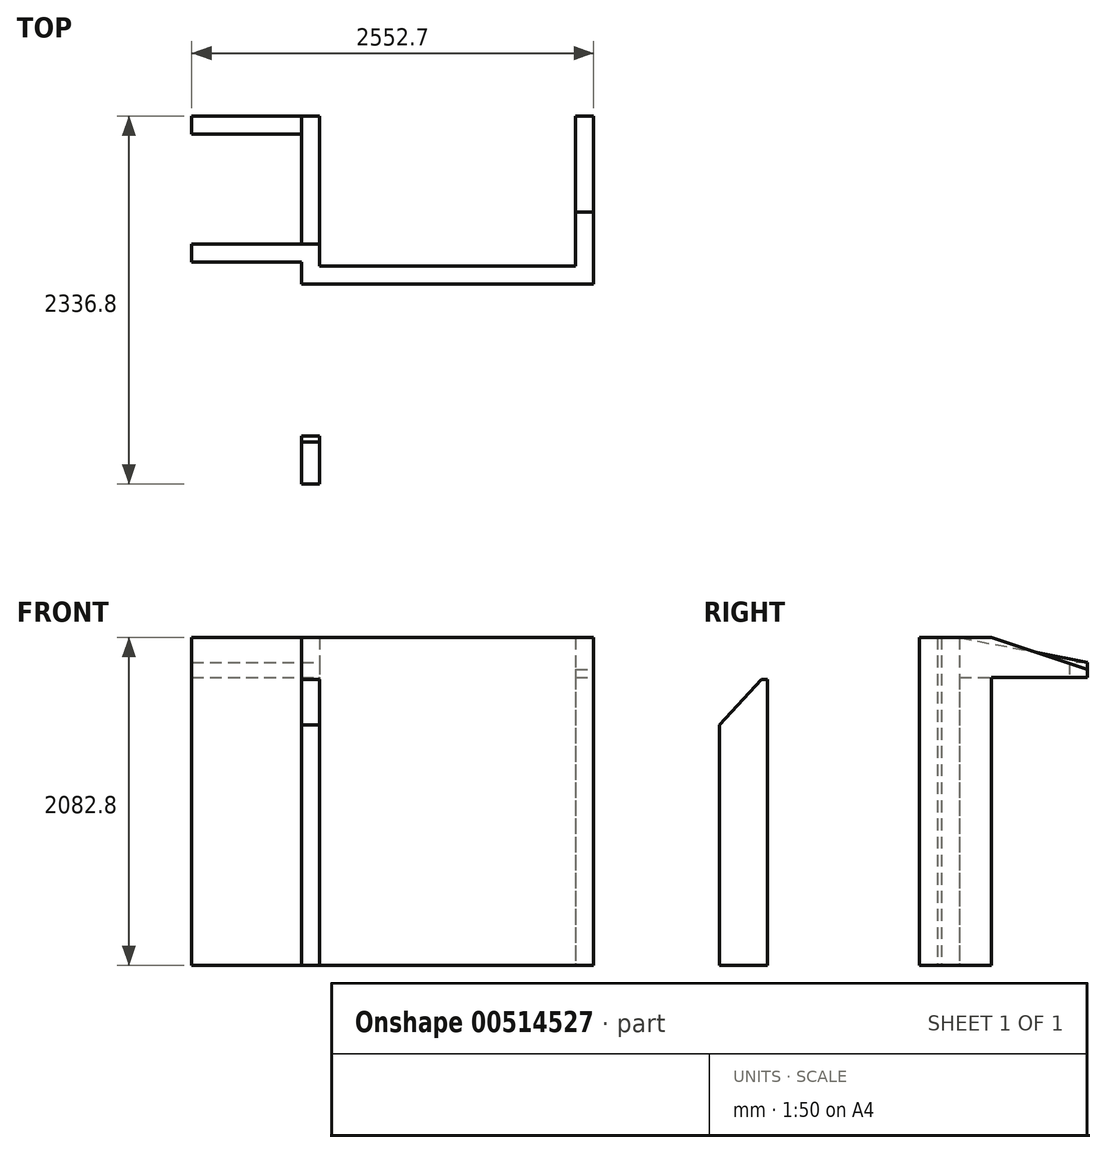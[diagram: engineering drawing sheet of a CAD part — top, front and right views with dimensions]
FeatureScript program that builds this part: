
annotation { "Feature Type Name" : "Feature", "Feature Type Description" : "" }
export const myFeature = defineFeature(function(context is Context, id is Id, definition is map)
    precondition{}
    {
        {
            var Q0;
            Q0=qCreatedBy(makeId("Top.planeOp"),FACE);
            var sketch = newSketch(context, id + "F0", { "sketchPlane" : qUnion([Q0])});
            skLineSegment(sketch, "E0.bottom", {"start": v(0, 0) * mm, "end": v(812.8, 0) * mm});
            skLineSegment(sketch, "E0.top", {"start": v(0, -114.3) * mm, "end": v(812.8, -114.3) * mm});
            skLineSegment(sketch, "E0.left", {"start": v(0, 0) * mm, "end": v(0, -114.3) * mm});
            skLineSegment(sketch, "E0.right", {"start": v(812.8, 0) * mm, "end": v(812.8, -114.3) * mm});
            skLineSegment(sketch, "E1.bottom", {"start": v(812.8, 0) * mm, "end": v(698.5, 0) * mm});
            skLineSegment(sketch, "E1.top", {"start": v(812.8, -254) * mm, "end": v(698.5, -254) * mm});
            skLineSegment(sketch, "E1.left", {"start": v(812.8, 0) * mm, "end": v(812.8, -254) * mm});
            skLineSegment(sketch, "E1.right", {"start": v(698.5, 0) * mm, "end": v(698.5, -254) * mm});
            skLineSegment(sketch, "E2.bottom", {"start": v(698.5, -254) * mm, "end": v(2552.7, -254) * mm});
            skLineSegment(sketch, "E2.top", {"start": v(698.5, -139.7) * mm, "end": v(2552.7, -139.7) * mm});
            skLineSegment(sketch, "E2.left", {"start": v(698.5, -254) * mm, "end": v(698.5, -139.7) * mm});
            skLineSegment(sketch, "E2.right", {"start": v(2552.7, -254) * mm, "end": v(2552.7, -139.7) * mm});
            skLineSegment(sketch, "E3.bottom", {"start": v(2552.7, -254) * mm, "end": v(2438.4, -254) * mm});
            skLineSegment(sketch, "E3.top", {"start": v(2552.7, 203.2) * mm, "end": v(2438.4, 203.2) * mm});
            skLineSegment(sketch, "E3.left", {"start": v(2552.7, -254) * mm, "end": v(2552.7, 203.2) * mm});
            skLineSegment(sketch, "E3.right", {"start": v(2438.4, -254) * mm, "end": v(2438.4, 203.2) * mm});
            skSolve(sketch);
        }
        {
            var Q0;
            Q0 = qSketchRegion(id + "F0", true);
            extrude(context, id + "F1", {"entities" : qUnion([Q0]), "depth" : 2082.8 * mm, "offsetDistance" : 25.4 * mm});
        }
        {
            var Q0;
            Q0=makeQuery(id+"F1.opExtrude","SWEPT_FACE",FACE,{"disambiguationData":[OSD([sQuery(id+"F0.wireOp",EDGE,"E1.right"),sQuery(id+"F0.wireOp",EDGE,"E2.left")])]});
            var sketch = newSketch(context, id + "F2", { "sketchPlane" : qUnion([Q0])});
            skLineSegment(sketch, "E4", {"start": v(254, 0) * mm, "end": v(1219.2, 0) * mm});
            skLineSegment(sketch, "E5.bottom", {"start": v(1219.2, 0) * mm, "end": v(1524, 0) * mm});
            skLineSegment(sketch, "E5.top", {"start": v(1219.2, 1816.1) * mm, "end": v(1524, 1816.1) * mm});
            skLineSegment(sketch, "E5.left", {"start": v(1219.2, 0) * mm, "end": v(1219.2, 1816.1) * mm});
            skLineSegment(sketch, "E5.right", {"start": v(1524, 0) * mm, "end": v(1524, 1816.1) * mm});
            skSolve(sketch);
        }
        {
            var Q0;
            Q0=makeQuery(id+"F2.imprint","IMPRINT",FACE,{"disambiguationData":[TD([[makeQuery(id+"F2.imprint","IMPRINT",EDGE,{"derivedFrom":sQuery(id+"F2.wireOp",EDGE,"E5.bottom")}),1.0]])]});
            extrude(context, id + "F3", {"entities" : qUnion([Q0]), "oppositeDirection" : true, "depth" : 114.3 * mm, "offsetDistance" : 25.4 * mm});
        }
        {
            var Q0;
            Q0=makeQuery(id+"F3.opExtrude","CAP_FACE",FACE,{"disambiguationData":[OSD([sQuery(id+"F2.wireOp",EDGE,"E5.bottom"),sQuery(id+"F2.wireOp",EDGE,"E5.top"),sQuery(id+"F2.wireOp",EDGE,"E5.left"),sQuery(id+"F2.wireOp",EDGE,"E5.right")])],"isStart":true});
            var sketch = newSketch(context, id + "F4", { "sketchPlane" : qUnion([Q0])});
            skLineSegment(sketch, "E6", {"start": v(1257.96, 1816.1) * mm, "end": v(1524, 1526.4) * mm});
            skLineSegment(sketch, "E7", {"start": v(1524, 1526.4) * mm, "end": v(1524, 1816.1) * mm});
            skLineSegment(sketch, "E8", {"start": v(1524, 1816.1) * mm, "end": v(1257.96, 1816.1) * mm});
            skSolve(sketch);
        }
        {
            var Q0;
            Q0=makeQuery(id+"F4.imprint","IMPRINT",FACE,{"disambiguationData":[TD([[makeQuery(id+"F4.imprint","IMPRINT",EDGE,{"derivedFrom":sQuery(id+"F4.wireOp",EDGE,"E6")}),1.0]])]});
            extrude(context, id + "F5", {"entities" : qUnion([Q0]), "operationType" : NewBodyOperationType.REMOVE, "oppositeDirection" : true, "depth" : 203.2 * mm, "offsetDistance" : 25.4 * mm});
        }
        {
            var Q0;
            Q0=makeQuery(id+"F1.opExtrude","SWEPT_FACE",FACE,{"disambiguationData":[OSD([sQuery(id+"F0.wireOp",EDGE,"E3.left")])]});
            var sketch = newSketch(context, id + "F6", { "sketchPlane" : qUnion([Q0])});
            skLineSegment(sketch, "E9", {"start": v(203.2, 0) * mm, "end": v(203.2, 1828.8) * mm});
            skLineSegment(sketch, "E10", {"start": v(203.2, 1828.8) * mm, "end": v(812.8, 1828.8) * mm});
            skLineSegment(sketch, "E11", {"start": v(203.2, 2082.8) * mm, "end": v(812.8, 1879.6) * mm});
            skLineSegment(sketch, "E12", {"start": v(812.8, 1879.6) * mm, "end": v(812.8, 1828.8) * mm});
            skSolve(sketch);
        }
        {
            var Q0;
            {var subQ0=sQuery(id+"F6.wireOp",EDGE,"E10");Q0=makeQuery(id+"F6.imprint","IMPRINT",FACE,{"disambiguationData":[TD([[makeQuery(id+"F6.imprint","IMPRINT",EDGE,{"derivedFrom":subQ0}),1.0]])]});}
            extrude(context, id + "F7", {"entities" : qUnion([Q0]), "operationType" : NewBodyOperationType.ADD, "oppositeDirection" : true, "depth" : 114.3 * mm, "offsetDistance" : 25.4 * mm});
        }
        {
            var Q0;
            Q0=makeQuery(id+"F1.opExtrude","SWEPT_FACE",FACE,{"disambiguationData":[OSD([sQuery(id+"F0.wireOp",EDGE,"E1.left")])]});
            var sketch = newSketch(context, id + "F8", { "sketchPlane" : qUnion([Q0])});
            skLineSegment(sketch, "E13", {"start": v(0, 0) * mm, "end": v(0, 1828.8) * mm});
            skLineSegment(sketch, "E14.top", {"start": v(0, 1828.8) * mm, "end": v(812.8, 1828.8) * mm});
            skLineSegment(sketch, "E14.left", {"start": v(0, 2082.8) * mm, "end": v(0, 1828.8) * mm});
            skLineSegment(sketch, "E14.right", {"start": v(812.8, 1924.25) * mm, "end": v(812.8, 1828.8) * mm});
            skLineSegment(sketch, "E15", {"start": v(0, 2082.8) * mm, "end": v(812.8, 1924.25) * mm});
            skSolve(sketch);
        }
        {
            var Q0;
            Q0=makeQuery(id+"F8.imprint","IMPRINT",FACE,{"disambiguationData":[TD([[makeQuery(id+"F8.imprint","IMPRINT",EDGE,{"derivedFrom":sQuery(id+"F8.wireOp",EDGE,"E14.top")}),1.0]])]});
            extrude(context, id + "F9", {"entities" : qUnion([Q0]), "operationType" : NewBodyOperationType.ADD, "oppositeDirection" : true, "depth" : 114.3 * mm, "offsetDistance" : 25.4 * mm});
        }
        {
            var Q0;
            Q0=makeQuery(id+"F9.opExtrude","CAP_FACE",FACE,{"disambiguationData":[OSD([sQuery(id+"F8.wireOp",EDGE,"E14.top"),sQuery(id+"F8.wireOp",EDGE,"E14.left"),sQuery(id+"F8.wireOp",EDGE,"E14.right"),sQuery(id+"F8.wireOp",EDGE,"E15")])],"isStart":false});
            var sketch = newSketch(context, id + "F10", { "sketchPlane" : qUnion([Q0])});
            skLineSegment(sketch, "E16.bottom", {"start": v(-812.8, 1924.25) * mm, "end": v(-698.5, 1924.25) * mm});
            skLineSegment(sketch, "E16.top", {"start": v(-812.8, 1828.8) * mm, "end": v(-698.5, 1828.8) * mm});
            skLineSegment(sketch, "E16.left", {"start": v(-812.8, 1924.25) * mm, "end": v(-812.8, 1828.8) * mm});
            skLineSegment(sketch, "E16.right", {"start": v(-698.5, 1924.25) * mm, "end": v(-698.5, 1828.8) * mm});
            skSolve(sketch);
        }
        {
            var Q0;
            Q0=makeQuery(id+"F10.imprint","IMPRINT",FACE,{"disambiguationData":[TD([[makeQuery(id+"F10.imprint","IMPRINT",EDGE,{"derivedFrom":sQuery(id+"F10.wireOp",EDGE,"E16.bottom")}),-1.0]])]});
            extrude(context, id + "F11", {"entities" : qUnion([Q0]), "operationType" : NewBodyOperationType.ADD, "depth" : 698.5 * mm, "offsetDistance" : 25.4 * mm});
        }
    });
